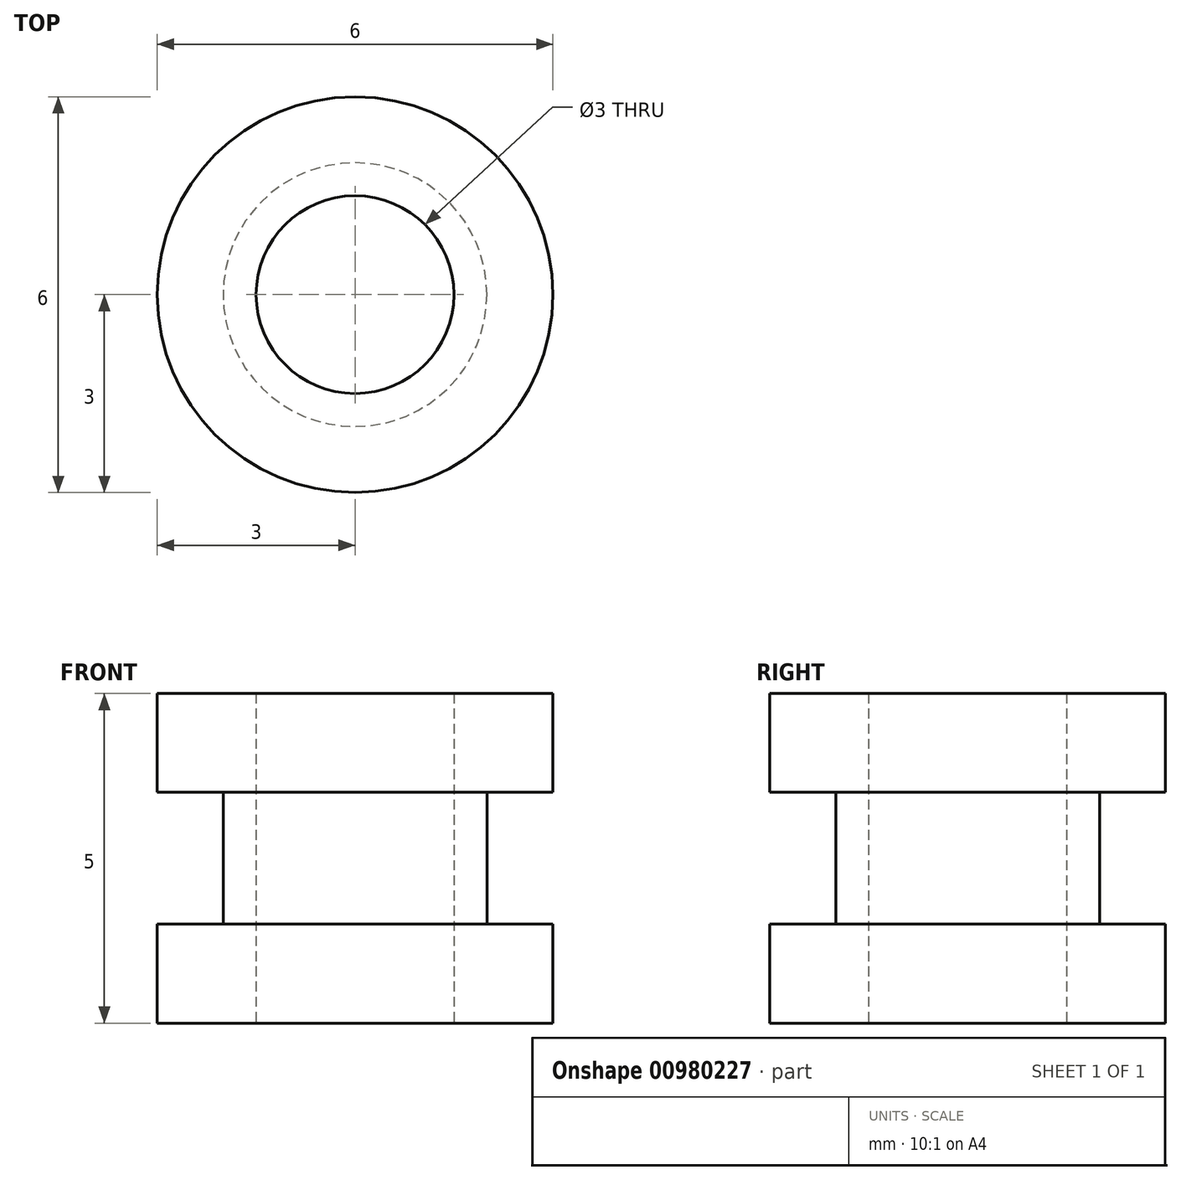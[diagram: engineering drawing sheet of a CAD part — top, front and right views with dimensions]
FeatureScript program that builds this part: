
annotation { "Feature Type Name" : "Feature", "Feature Type Description" : "" }
export const myFeature = defineFeature(function(context is Context, id is Id, definition is map)
    precondition{}
    {
        {
            var Q0;
            Q0=qCreatedBy(makeId("Front.planeOp"),FACE);
            var sketch = newSketch(context, id + "F0", { "sketchPlane" : qUnion([Q0])});
            skPoint(sketch, "E0", {"position": v(0, 2.5) * mm});
            skPoint(sketch, "E1", {"position": v(3, 1) * mm});
            skPoint(sketch, "E2", {"position": v(3, 2.5) * mm});
            skPoint(sketch, "E3", {"position": v(1.5, 1) * mm});
            skPoint(sketch, "E4", {"position": v(1.5, 0) * mm});
            skPoint(sketch, "E5", {"position": v(2, 0) * mm});
            skPoint(sketch, "E6", {"position": v(2, 1) * mm});
            skPoint(sketch, "E7", {"position": v(1.5, 2.5) * mm});
            skLineSegment(sketch, "E8", {"start": v(3, 2.5) * mm, "end": v(1.5, 2.5) * mm});
            skLineSegment(sketch, "E9", {"start": v(1.5, 2.5) * mm, "end": v(1.5, 0) * mm});
            skLineSegment(sketch, "E10", {"start": v(2, 0) * mm, "end": v(2, 1) * mm});
            skLineSegment(sketch, "E11", {"start": v(3, 1) * mm, "end": v(2, 1) * mm});
            skLineSegment(sketch, "E12", {"start": v(3, 1) * mm, "end": v(3, 2.5) * mm});
            skPoint(sketch, "E13.MirrorP", {"position": v(1.5, -1) * mm});
            skPoint(sketch, "E14.MirrorP", {"position": v(2, -1) * mm});
            skLineSegment(sketch, "E15.MirrorCS", {"start": v(2, 0) * mm, "end": v(2, -1) * mm});
            skPoint(sketch, "E16.MirrorP", {"position": v(3, -1) * mm});
            skLineSegment(sketch, "E17.MirrorCS", {"start": v(1.5, -2.5) * mm, "end": v(1.5, 0) * mm});
            skPoint(sketch, "E18.MirrorP", {"position": v(1.5, -2.5) * mm});
            skLineSegment(sketch, "E19.MirrorCS", {"start": v(3, -2.5) * mm, "end": v(1.5, -2.5) * mm});
            skLineSegment(sketch, "E20.MirrorCS", {"start": v(3, -1) * mm, "end": v(2, -1) * mm});
            skLineSegment(sketch, "E21.MirrorCS", {"start": v(3, -1) * mm, "end": v(3, -2.5) * mm});
            skPoint(sketch, "E22.MirrorP", {"position": v(3, -2.5) * mm});
            skLineSegment(sketch, "E23", {"start": v(0, 0) * mm, "end": v(0, 2.5) * mm, "construction": true});
            skSolve(sketch);
        }
        {
            var Q0;
            Q0 = qSketchRegion(id + "F0", true);
            var Q1;
            Q1=sQuery(id+"F0.wireOp",EDGE,"E23");
            revolve(context, id + "F1", {"surfaceOperationType" : NewSurfaceOperationType.NEW, "entities" : qUnion([Q0]), "axis" : qUnion([Q1]), "revolveType" : RevolveType.FULL});
        }
    });
